# Revit family: 1STERN_MIXING_VALVE_UNDERBASIN_TMW
name_source: partatom
category: Generic Models
revit_build: Autodesk Revit 2017 (Build: 20160225_1515(x64)
units: mm (PartAtom-declared; Revit-internal decimal feet)

## family parameters
Can host rebar = No
Cut with Voids When Loaded = No
Host = Face
Part Type = Normal
Room Calculation Point = Yes
Round Connector Dimension = Use Diameter
Shared = No

## types (1)
- UNDERBASIN TMW
    AVAILABLE FINISHES = Brushed Nickel - Matt Black - Satin Gold - PVD Antique Bronze - PVD rose Gold - PVD Copper - AISI316 Material
    BADGE = https://bim.archiproducts.com
    DEPTH = 75 mm
    Default Elevation = 1219 mm
    Description = Mixer Thermostatic Tap for public WC - This high quality, lead-free, brass, pre-mixing unit is a thermostatic mixing valve that allows easy adjustment of hot and cold water by connecting directly to the angle valves under the basin.‎ Includes a hot water stop function to prevent scalding.‎ Includes built-in filters to prevent dirt entering the system.‎ Includes back check valves to prevent hot water entering the cold water inlet.‎ Connection kit available upon request.‎
    FINISHING MATERIAL = Chrome - Stern
    HEIGHT = 100 mm  [stored 0.328084 ft]
    INSTALLATION = Below deck
    MATERIAL DESCRIPTION = Finish: Chrome
    Manufacturer = Stern Engineering
    Model = Underbasin TMV
    OPERATING PRESSURE = 1.0 - 5.0 BAR (14.5 - 72.5 PSI)
    PRE-SET TEMPERATURE = 38°C / 100°F
    PRODUCT CODE = 7200069
    PRODUCT SHEET = https://www.archiproducts.com
    TECHNICAL SHEET = http://www.sternfaucets.com
    TEMPERATURE RANGE = 15-70°C / 59°-158°F
    Type Comments = G 3/8" inlet
    URL = http://www.sternfaucets.com
    WATER FLOW = 25.0 LPM
    WATER SUPPLY = Cold or hot water
    WATER TEMPERATURE = 80°C / 176°F Maximum
    WIDTH = 35 mm  [stored 0.114829 ft]

note: [stored X ft] marks values corroborated as IEEE doubles in the binary element streams (Revit-internal decimal feet)

## geometry (parser evidence)
native form markers: Sweep x2
no freeform markers — native parametric forms only
